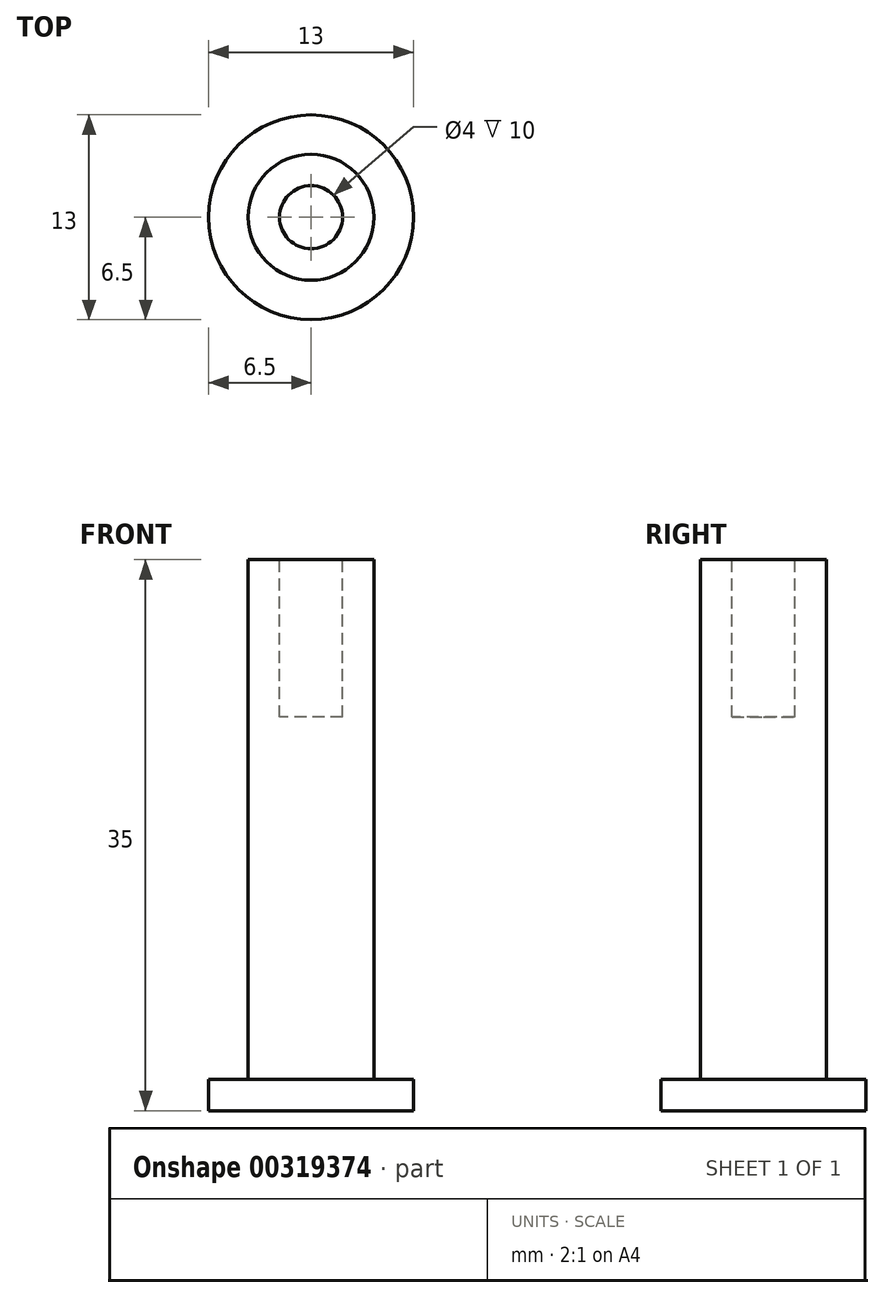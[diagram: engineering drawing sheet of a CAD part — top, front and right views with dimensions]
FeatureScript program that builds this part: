
annotation { "Feature Type Name" : "Feature", "Feature Type Description" : "" }
export const myFeature = defineFeature(function(context is Context, id is Id, definition is map)
    precondition{}
    {
        {
            var Q0;
            Q0=qCreatedBy(makeId("Top.planeOp"),FACE);
            var sketch = newSketch(context, id + "F0", { "sketchPlane" : qUnion([Q0])});
            skCircle(sketch, "E0", {"center": v(0, 0) * mm, "radius": 4 * mm});
            skSolve(sketch);
        }
        {
            var Q0;
            Q0=makeQuery(id+"F0.imprint","IMPRINT",FACE,{"disambiguationData":[TD([[makeQuery(id+"F0.imprint","IMPRINT",EDGE,{"derivedFrom":sQuery(id+"F0.wireOp",EDGE,"E0")}),1.0]])]});
            extrude(context, id + "F1", {"entities" : qUnion([Q0]), "depth" : 33 * mm});
        }
        {
            var Q0;
            Q0=makeQuery(id+"F1.opExtrude","CAP_FACE",FACE,{"disambiguationData":[OSD([sQuery(id+"F0.wireOp",EDGE,"E0")])],"isStart":true});
            var sketch = newSketch(context, id + "F2", { "sketchPlane" : qUnion([Q0])});
            skCircle(sketch, "E1", {"center": v(0, 0) * mm, "radius": 6.5 * mm});
            skSolve(sketch);
        }
        {
            var Q0;
            Q0 = qSketchRegion(id + "F2", true);
            extrude(context, id + "F3", {"entities" : qUnion([Q0]), "operationType" : NewBodyOperationType.ADD, "depth" : 2 * mm});
        }
        {
            var Q0;
            Q0=makeQuery(id+"F1.opExtrude","CAP_FACE",FACE,{"disambiguationData":[OSD([sQuery(id+"F0.wireOp",EDGE,"E0")])],"isStart":false});
            var sketch = newSketch(context, id + "F4", { "sketchPlane" : qUnion([Q0])});
            skCircle(sketch, "E2", {"center": v(0, 0) * mm, "radius": 2 * mm});
            skSolve(sketch);
        }
        {
            var Q0;
            Q0 = qSketchRegion(id + "F4", true);
            extrude(context, id + "F5", {"entities" : qUnion([Q0]), "operationType" : NewBodyOperationType.REMOVE, "oppositeDirection" : true, "depth" : 10 * mm});
        }
    });
